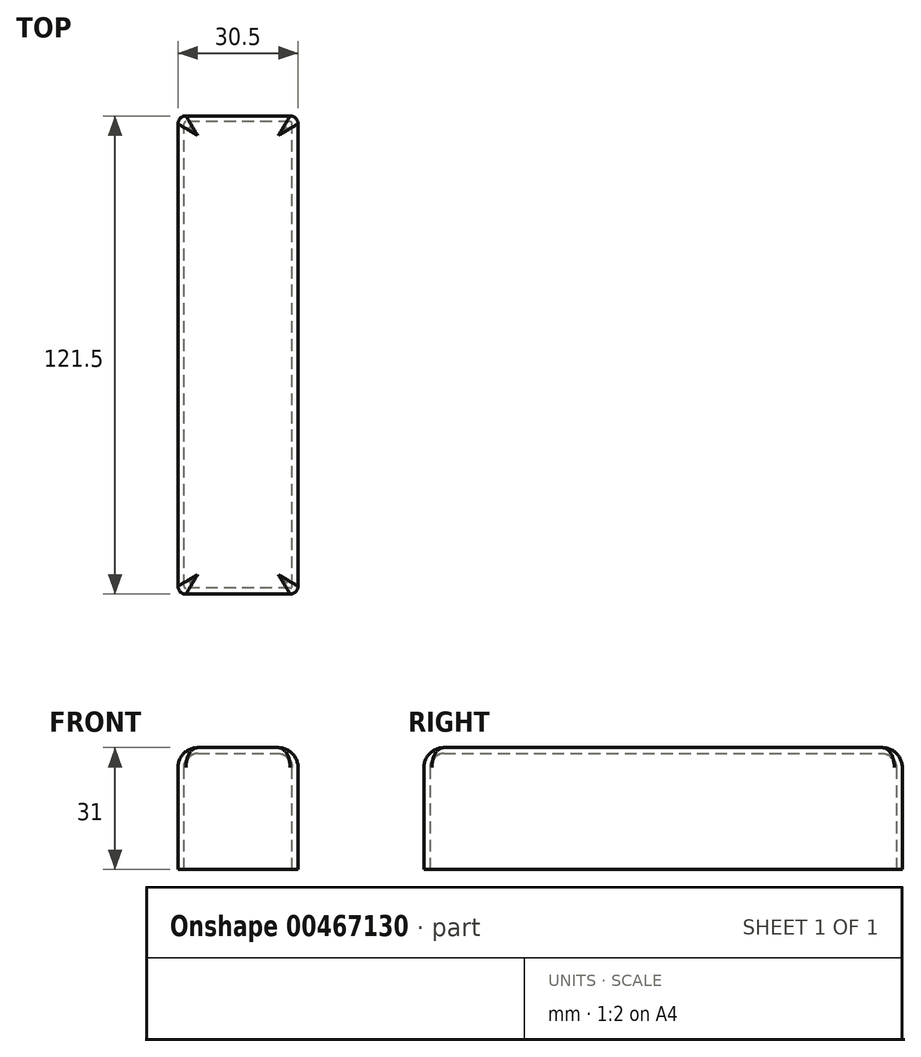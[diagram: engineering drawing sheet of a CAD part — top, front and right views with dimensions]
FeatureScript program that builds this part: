
annotation { "Feature Type Name" : "Feature", "Feature Type Description" : "" }
export const myFeature = defineFeature(function(context is Context, id is Id, definition is map)
    precondition{}
    {
        {
            var Q0;
            Q0=qCreatedBy(makeId("Top.planeOp"),FACE);
            var sketch = newSketch(context, id + "F0", { "sketchPlane" : qUnion([Q0])});
            skLineSegment(sketch, "E0.bottom", {"start": v(15.25, -60.75) * mm, "end": v(-15.25, -60.75) * mm});
            skLineSegment(sketch, "E0.top", {"start": v(15.25, 60.75) * mm, "end": v(-15.25, 60.75) * mm});
            skLineSegment(sketch, "E0.left", {"start": v(15.25, -60.75) * mm, "end": v(15.25, 60.75) * mm});
            skLineSegment(sketch, "E0.right", {"start": v(-15.25, -60.75) * mm, "end": v(-15.25, 60.75) * mm});
            skPoint(sketch, "E0.middle", {"position": v(0, 0) * mm});
            skSolve(sketch);
        }
        {
            var Q0;
            Q0=makeQuery(id+"F0.imprint","IMPRINT",FACE,{"disambiguationData":[TD([[makeQuery(id+"F0.imprint","IMPRINT",EDGE,{"derivedFrom":sQuery(id+"F0.wireOp",EDGE,"E0.bottom")}),-1.0]])]});
            extrude(context, id + "F1", {"entities" : qUnion([Q0]), "depth" : 31 * mm});
        }
        {
            var Q0;
            Q0=makeQuery(id+"F1.opExtrude","SWEPT_EDGE",EDGE,{"disambiguationData":[OSD([sQuery(id+"F0.wireOp",EDGE,"E0.top"),sQuery(id+"F0.wireOp",EDGE,"E0.left")])]});
            var Q1;
            Q1=makeQuery(id+"F1.opExtrude","SWEPT_EDGE",EDGE,{"disambiguationData":[OSD([sQuery(id+"F0.wireOp",EDGE,"E0.top"),sQuery(id+"F0.wireOp",EDGE,"E0.right")])]});
            var Q2;
            Q2=makeQuery(id+"F1.opExtrude","SWEPT_EDGE",EDGE,{"disambiguationData":[OSD([sQuery(id+"F0.wireOp",EDGE,"E0.bottom"),sQuery(id+"F0.wireOp",EDGE,"E0.right")])]});
            var Q3;
            Q3=makeQuery(id+"F1.opExtrude","SWEPT_EDGE",EDGE,{"disambiguationData":[OSD([sQuery(id+"F0.wireOp",EDGE,"E0.bottom"),sQuery(id+"F0.wireOp",EDGE,"E0.left")])]});
            fillet(context, id + "F2", {"entities" : qUnion([Q0, Q1, Q2, Q3]), "radius" : 2 * mm, "tangentPropagation" : true, "allowEdgeOverflow" : false});
        }
        {
            var Q0;
            Q0=makeQuery(id+"F1.opExtrude","CAP_EDGE",EDGE,{"disambiguationData":[OSD([sQuery(id+"F0.wireOp",EDGE,"E0.right")])],"isStart":false});
            fillet(context, id + "F3", {"entities" : qUnion([Q0]), "radius" : 5 * mm, "tangentPropagation" : true, "allowEdgeOverflow" : false});
        }
        {
            var Q0;
            Q0=makeQuery(id+"F1.opExtrude","CAP_FACE",FACE,{"disambiguationData":[OSD([sQuery(id+"F0.wireOp",EDGE,"E0.bottom"),sQuery(id+"F0.wireOp",EDGE,"E0.top"),sQuery(id+"F0.wireOp",EDGE,"E0.left"),sQuery(id+"F0.wireOp",EDGE,"E0.right")])],"isStart":true});
            shell(context, id + "F4", {"entities" : qUnion([Q0]), "thickness" : 1.5 * mm});
        }
    });
